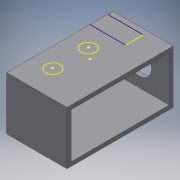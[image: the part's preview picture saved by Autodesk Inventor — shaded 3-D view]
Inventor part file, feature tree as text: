
AUTODESK INVENTOR PART (.ipt)
format: ipt  version: 2018 (Build 220112000, 112)  size: 116,736 bytes
history: native  units: mm
features: other x7, sketch x4, reference x3, extrude x2, hole x1
ambient origin geometry x8: Origin, YZ Plane, XZ Plane, XY Plane, X Axis, Y Axis, Z Axis, Center Point
bodies: Body1 (feature_tree)
feature tree (17):
  other  "ソリッド1"
  extrude  "押し出し1"  Depth=60.0mm
  extrude  "押し出し2"  Depth=30.0mm
  sketch  "スケッチ3"
  hole  "穴1"  [1 undecoded]
  sketch  "スケッチ1"
  sketch  "スケッチ2"
  reference  "参照1"
  sketch  "スケッチ4"
  reference  "参照2"
  reference  "参照3"
  other  "<userpath>\Documents\RBBR\CAD\カート.iam"
  other  "カート.iam"
  other  "後輪:2"
  other  "<userpath>\Documents\RBBR\CAD\サスペンション\車軸受け(後,左).iam"
  other  "車軸受け(後,左).iam"
  other  "ブレーキ固定アングル:1"
note: 1 required parameter value undecoded (feature->parameter linkage not recoverable at this tier; creation-order binding heuristic only, values carry confidence <= 0.55)
